# Revit family: S300
name_source: partatom
category: Modelos genéricos
revit_build: Autodesk Revit 2017 (Build: 20170118_1100(x64)
units: mm (PartAtom-declared; Revit-internal decimal feet)

## family parameters
Compartido = No
Corte con vacíos al cargar = No
Cota de conector redondo = Diámetro de uso
Puede alojar armadura = No
Punto de cálculo de habitación = No
Tipo de pieza = Normal

## types (2) — shared parameters
Altura = 210 mm  [stored 0.688976 ft]
Anchura exterior = 312 mm  [stored 1.02362 ft]
Anchura interior = 250 mm  [stored 0.82021 ft]
Caudal de referencia = 22 L/s
Clase de carga = F-900 Norma EN-1433
Descripción = Canal de Hormigón Polímero tipo ULMA / modelo S300F-MF / ancho exterior 312mm / ancho interior 250mm y con alturas exteriores disponibles de 210mm / para recogida de aguas pluviales / en módulos de 1 ML de longitud / fijación de seguridad en 8 puntos por ML / perfiles de acero galvanizado* para protección lateral.
Fabricante = ULMA Architectural
Ficha técnica = http://www.ulmaarchitectural.com
Pendiente = 0.00%
Sección hidráulica = 407.00 cm²
URL = http://www.ulmaarchitectural.com
Ø salida horizontal = 0 mm
Ø salida vertical = 200 mm

## per-type parameters (varying)
| type | Costo | Peso |
| S300F | 99.09€ | 34.57 kg |
| S300MF | 119.51€ | 35.31 kg |

note: column(s) folded — value = type name in every type: Modelo

note: [stored X ft] marks values corroborated as IEEE doubles in the binary element streams (Revit-internal decimal feet)
